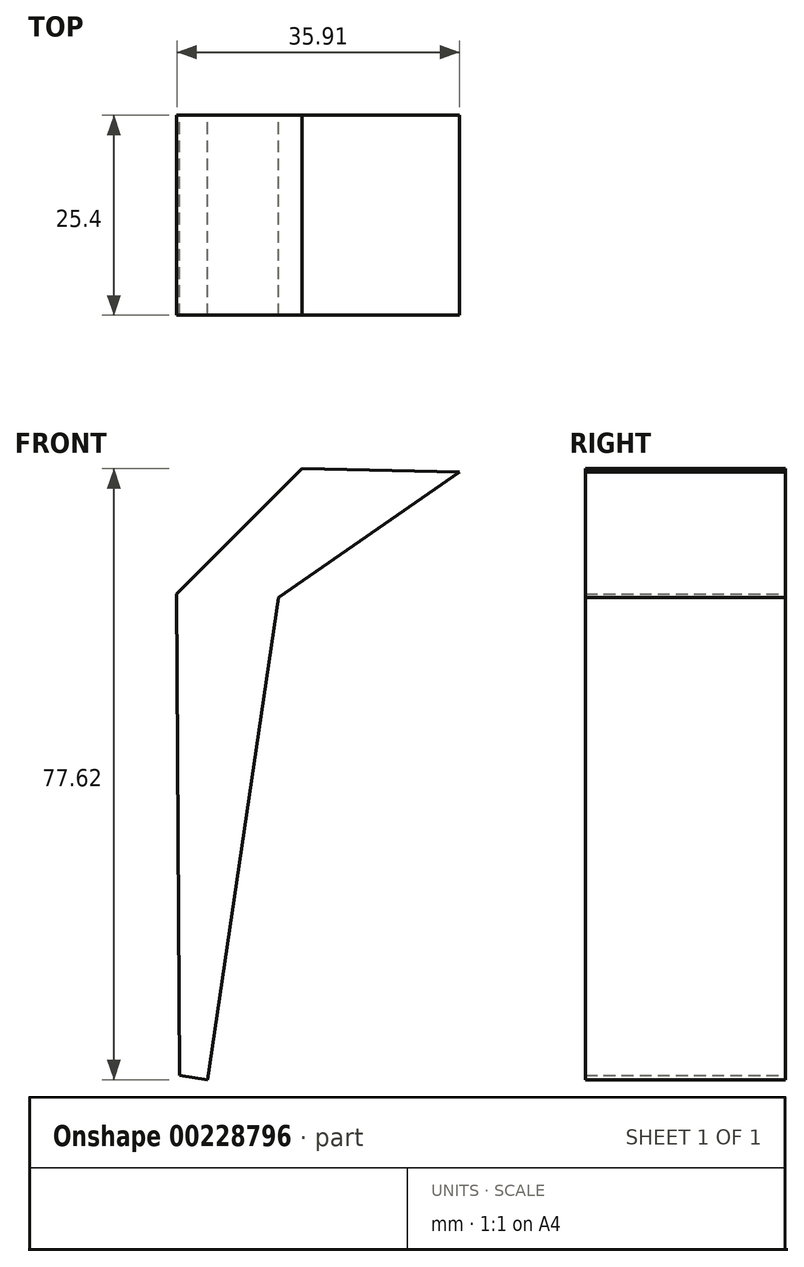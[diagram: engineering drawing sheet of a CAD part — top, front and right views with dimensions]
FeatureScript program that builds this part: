
annotation { "Feature Type Name" : "Feature", "Feature Type Description" : "" }
export const myFeature = defineFeature(function(context is Context, id is Id, definition is map)
    precondition{}
    {
        {
            var Q0;
            Q0=qCreatedBy(makeId("Front.planeOp"),FACE);
            var sketch = newSketch(context, id + "F0", { "sketchPlane" : qUnion([Q0])});
            skLineSegment(sketch, "E0", {"start": v(0.22, -0.05) * mm, "end": v(-0.11, 61.65) * mm});
            skLineSegment(sketch, "E1", {"start": v(-0.11, 61.65) * mm, "end": v(15.8, 77.57) * mm});
            skLineSegment(sketch, "E2", {"start": v(15.8, 77.57) * mm, "end": v(35.8, 77.12) * mm});
            skLineSegment(sketch, "E3", {"start": v(35.8, 77.12) * mm, "end": v(12.82, 61.2) * mm});
            skLineSegment(sketch, "E4", {"start": v(12.82, 61.2) * mm, "end": v(3.77, -0.05) * mm});
            skLineSegment(sketch, "E5", {"start": v(3.77, -0.05) * mm, "end": v(-0.45, 0.58) * mm});
            skSolve(sketch);
        }
        {
            var Q0;
            Q0 = qSketchRegion(id + "F0", true);
            extrude(context, id + "F1", {"entities" : qUnion([Q0]), "depth" : 25.4 * mm});
        }
    });
